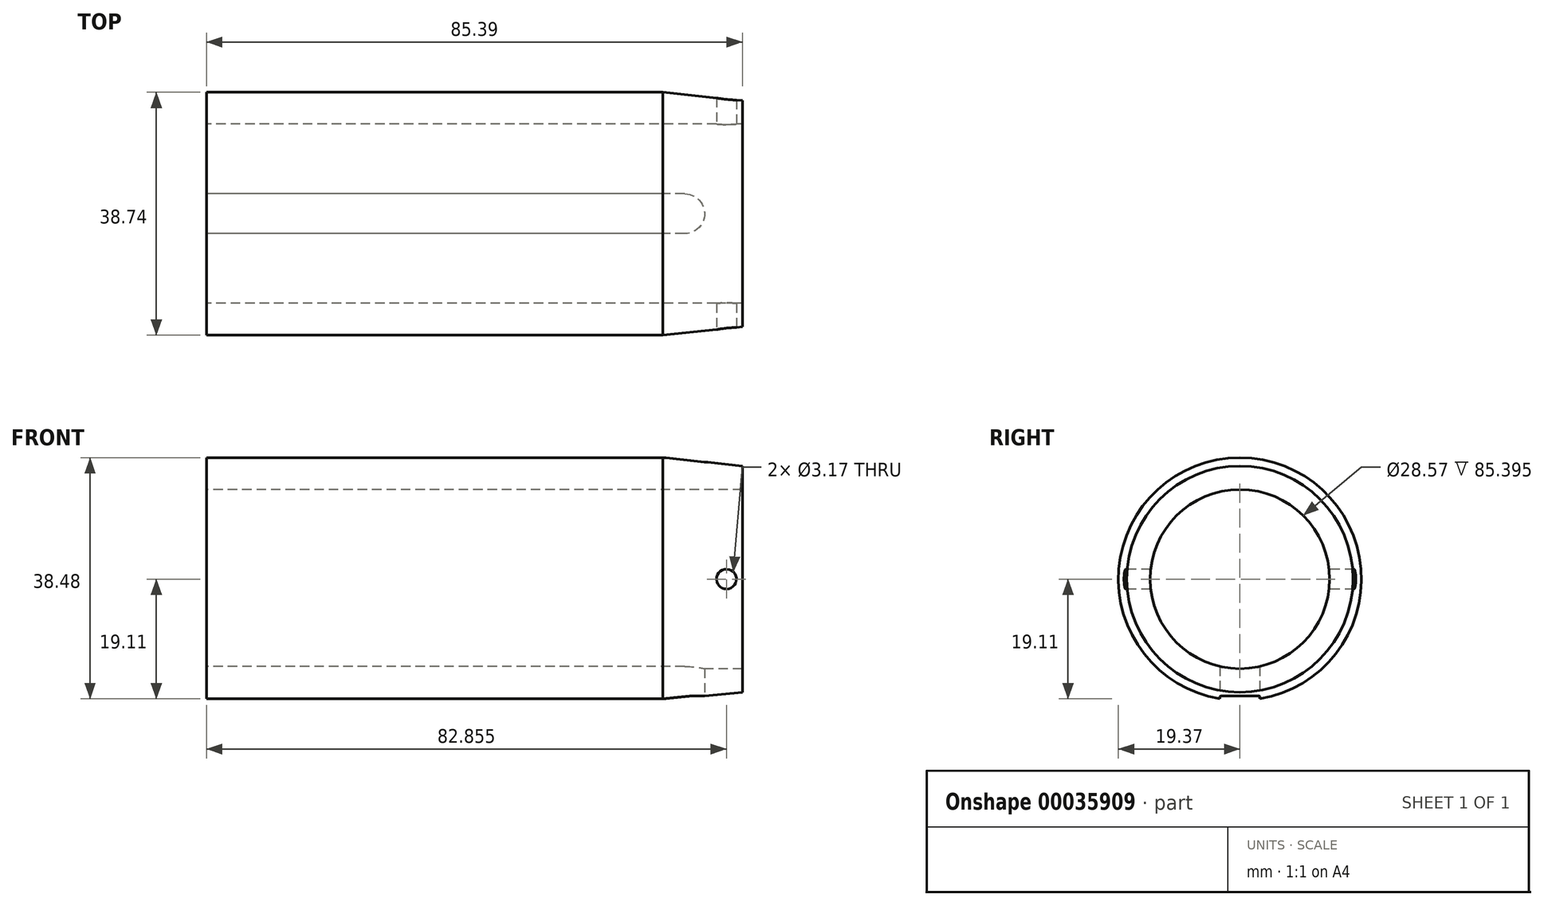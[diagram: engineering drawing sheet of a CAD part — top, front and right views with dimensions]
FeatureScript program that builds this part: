
annotation { "Feature Type Name" : "Feature", "Feature Type Description" : "" }
export const myFeature = defineFeature(function(context is Context, id is Id, definition is map)
    precondition{}
    {
        {
            var Q0;
            Q0=qCreatedBy(makeId("Front.planeOp"),FACE);
            var sketch = newSketch(context, id + "F0", { "sketchPlane" : qUnion([Q0])});
            skLineSegment(sketch, "E0", {"start": v(0, 0) * mm, "end": v(85.4, 0) * mm, "construction": true});
            skLineSegment(sketch, "E1", {"start": v(0, 19.37) * mm, "end": v(0, 14.29) * mm});
            skLineSegment(sketch, "E2", {"start": v(0, 14.29) * mm, "end": v(85.4, 14.29) * mm});
            skLineSegment(sketch, "E3", {"start": v(85.4, 14.29) * mm, "end": v(85.4, 18.03) * mm});
            skLineSegment(sketch, "E4", {"start": v(85.4, 18.03) * mm, "end": v(72.7, 19.37) * mm});
            skLineSegment(sketch, "E5", {"start": v(72.7, 19.37) * mm, "end": v(0, 19.37) * mm});
            skSolve(sketch);
        }
        {
            var Q0;
            Q0=makeQuery(id+"F0.imprint","IMPRINT",FACE,{"disambiguationData":[TD([[makeQuery(id+"F0.imprint","IMPRINT",EDGE,{"derivedFrom":sQuery(id+"F0.wireOp",EDGE,"E1")}),1.0]])]});
            var Q1;
            Q1=sQuery(id+"F0.wireOp",EDGE,"E0");
            revolve(context, id + "F1", {"entities" : qUnion([Q0]), "axis" : qUnion([Q1]), "revolveType" : RevolveType.FULL});
        }
        {
            var Q0;
            Q0=qCreatedBy(makeId("Front.planeOp"),FACE);
            var sketch = newSketch(context, id + "F2", { "sketchPlane" : qUnion([Q0])});
            skCircle(sketch, "E6", {"center": v(82.85, 0) * mm, "radius": 1.59 * mm});
            skSolve(sketch);
        }
        {
            var Q0;
            Q0 = qSketchRegion(id + "F2", true);
            extrude(context, id + "F3", {"entities" : qUnion([Q0]), "operationType" : NewBodyOperationType.REMOVE, "endBound" : BoundingType.THROUGH_ALL, "oppositeDirection" : true, "depth" : 25.4 * mm, "hasSecondDirection" : true, "secondDirectionBound" : BoundingType.THROUGH_ALL, "secondDirectionOppositeDirection" : false, "secondDirectionDepth" : 25.4 * mm});
        }
        {
            var Q0;
            Q0=makeQuery(id+"F1.opRevolve","SWEPT_FACE",FACE,{"disambiguationData":[OSD([sQuery(id+"F0.wireOp",EDGE,"E1")])]});
            var sketch = newSketch(context, id + "F4", { "sketchPlane" : qUnion([Q0])});
            skPoint(sketch, "E7", {"position": v(0, -19.37) * mm});
            skSolve(sketch);
        }
        {
            var Q0;
            Q0=qCreatedBy(makeId("Top.planeOp"),FACE);
            var Q1;
            Q1=sQuery(id+"F4.wireOp",VERTEX,"E7");
            cPlane(context, id + "F5", {"entities" : qUnion([Q0, Q1]), "cplaneType" : CPlaneType.PLANE_POINT, "offset" : 152.4 * mm, "width" : 152.4 * mm, "height" : 152.4 * mm});
        }
        {
            var Q0;
            Q0=qCreatedBy(id+"F5.planeOp",FACE);
            var sketch = newSketch(context, id + "F6", { "sketchPlane" : qUnion([Q0])});
            skLineSegment(sketch, "E8.rect.bottom", {"start": v(0, 3.18) * mm, "end": v(76.2, 3.18) * mm});
            skLineSegment(sketch, "E8.rect.top", {"start": v(0, -3.17) * mm, "end": v(76.2, -3.17) * mm});
            skLineSegment(sketch, "E8.rect.left", {"start": v(0, 3.18) * mm, "end": v(0, -3.17) * mm});
            skLineSegment(sketch, "E8.rect.right", {"start": v(76.2, 3.17) * mm, "end": v(76.2, -3.17) * mm});
            skPoint(sketch, "E8.rect.middle", {"position": v(38.1, 0) * mm});
            skArc(sketch, "E9", {"start": v(76.2, -3.17) * mm, "mid": v(79.38, 0) * mm, "end": v(76.2, 3.17) * mm});
            skSolve(sketch);
        }
        {
            var Q0;
            Q0 = qSketchRegion(id + "F6", true);
            extrude(context, id + "F7", {"entities" : qUnion([Q0]), "operationType" : NewBodyOperationType.REMOVE, "endBound" : BoundingType.UP_TO_NEXT, "depth" : 25.4 * mm});
        }
    });
